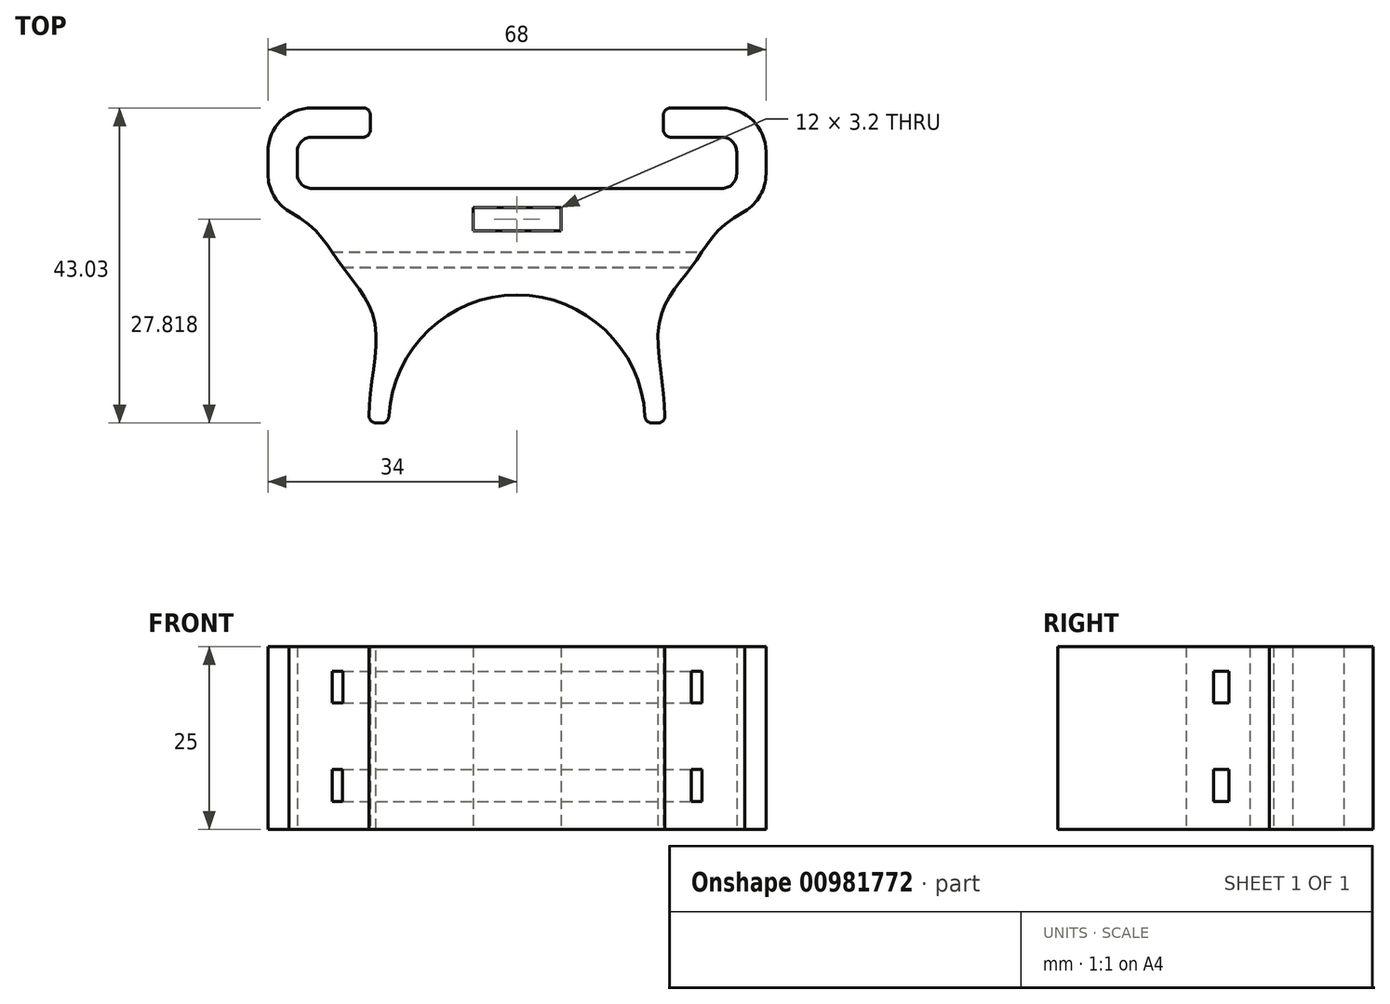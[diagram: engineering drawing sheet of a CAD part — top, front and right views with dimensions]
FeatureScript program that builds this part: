
annotation { "Feature Type Name" : "Feature", "Feature Type Description" : "" }
export const myFeature = defineFeature(function(context is Context, id is Id, definition is map)
    precondition{}
    {
        {
            var Q0;
            Q0=qCreatedBy(makeId("Top.planeOp"),FACE);
            var sketch = newSketch(context, id + "F0", { "sketchPlane" : qUnion([Q0])});
            skLineSegment(sketch, "E0", {"start": v(0, 0) * mm, "end": v(28, 0) * mm});
            skLineSegment(sketch, "E1", {"start": v(30, 2) * mm, "end": v(30, 5) * mm});
            skLineSegment(sketch, "E2", {"start": v(28, 7) * mm, "end": v(21, 7) * mm});
            skPoint(sketch, "E3.visualSharp", {"position": v(30, 7) * mm});
            skArc(sketch, "E3.filletArc", {"start": v(30, 5) * mm, "mid": v(29.41, 6.41) * mm, "end": v(28, 7) * mm});
            skPoint(sketch, "E4.visualSharp", {"position": v(30, 0) * mm});
            skArc(sketch, "E4.filletArc", {"start": v(28, 0) * mm, "mid": v(29.41, 0.59) * mm, "end": v(30, 2) * mm});
            skLineSegment(sketch, "E5.0", {"start": v(28, 11) * mm, "end": v(21, 11) * mm});
            skArc(sketch, "E5.2", {"start": v(31.12, -3.13) * mm, "mid": v(33.23, -0.94) * mm, "end": v(34, 2) * mm});
            skLineSegment(sketch, "E5.3", {"start": v(34, 2) * mm, "end": v(34, 5) * mm});
            skArc(sketch, "E5.4", {"start": v(34, 5) * mm, "mid": v(32.24, 9.24) * mm, "end": v(28, 11) * mm});
            skLineSegment(sketch, "E6", {"start": v(20, 10) * mm, "end": v(20, 8) * mm});
            skPoint(sketch, "E7.visualSharp", {"position": v(20, 11) * mm});
            skArc(sketch, "E7.filletArc", {"start": v(21, 11) * mm, "mid": v(20.3, 10.7) * mm, "end": v(20, 10) * mm});
            skPoint(sketch, "E8.visualSharp", {"position": v(20, 7) * mm});
            skArc(sketch, "E8.filletArc", {"start": v(20, 8) * mm, "mid": v(20.3, 7.3) * mm, "end": v(21, 7) * mm});
            skArc(sketch, "E9", {"start": v(17.47, -31.08) * mm, "mid": v(12.04, -19.32) * mm, "end": v(0, -14.53) * mm});
            skLineSegment(sketch, "E10", {"start": v(18.47, -32.03) * mm, "end": v(19.2, -32.03) * mm});
            skFitSpline(sketch, "E11", {"points": [v(20.16, -32.03) * mm, v(19.44, -18.28) * mm, v(24.17, -10.26) * mm, v(31.12, -3.13) * mm], "startDerivative": vector(2.72, 32.22) * mm, "endDerivative": vector(38.57, 19.7) * mm});
            skPoint(sketch, "E12.visualSharp", {"position": v(17.5, -32.03) * mm});
            skArc(sketch, "E12.filletArc", {"start": v(17.47, -31.08) * mm, "mid": v(17.79, -31.75) * mm, "end": v(18.47, -32.03) * mm});
            skArc(sketch, "E13.filletArc", {"start": v(19.2, -32.03) * mm, "mid": v(19.9, -31.74) * mm, "end": v(20.2, -31.03) * mm});
            skLineSegment(sketch, "E14.bottom", {"start": v(0, -2.61) * mm, "end": v(6, -2.61) * mm});
            skLineSegment(sketch, "E14.right", {"start": v(6, -2.61) * mm, "end": v(6, -5.81) * mm});
            skLineSegment(sketch, "E15", {"start": v(0, 0) * mm, "end": v(0, -2.61) * mm});
            skArc(sketch, "E16.MirrorCS", {"start": v(-19.2, -32.03) * mm, "mid": v(-19.9, -31.74) * mm, "end": v(-20.2, -31.03) * mm});
            skLineSegment(sketch, "E17.MirrorCS", {"start": v(-18.47, -32.03) * mm, "end": v(-19.2, -32.03) * mm});
            skArc(sketch, "E18.MirrorCS", {"start": v(-17.47, -31.08) * mm, "mid": v(-17.79, -31.75) * mm, "end": v(-18.47, -32.03) * mm});
            skArc(sketch, "E19.MirrorCS", {"start": v(-20, 8) * mm, "mid": v(-20.3, 7.3) * mm, "end": v(-21, 7) * mm});
            skLineSegment(sketch, "E20.MirrorCS", {"start": v(-20, 10) * mm, "end": v(-20, 8) * mm});
            skArc(sketch, "E21.MirrorCS", {"start": v(-21, 11) * mm, "mid": v(-20.3, 10.7) * mm, "end": v(-20, 10) * mm});
            skArc(sketch, "E22.MirrorCS", {"start": v(-30, 5) * mm, "mid": v(-29.41, 6.41) * mm, "end": v(-28, 7) * mm});
            skArc(sketch, "E23.MirrorCS", {"start": v(-28, 0) * mm, "mid": v(-29.41, 0.59) * mm, "end": v(-30, 2) * mm});
            skLineSegment(sketch, "E24.MirrorCS", {"start": v(-34, 2) * mm, "end": v(-34, 5) * mm});
            skArc(sketch, "E25.MirrorCS", {"start": v(-31.12, -3.13) * mm, "mid": v(-33.23, -0.94) * mm, "end": v(-34, 2) * mm});
            skArc(sketch, "E26.MirrorCS", {"start": v(-34, 5) * mm, "mid": v(-32.24, 9.24) * mm, "end": v(-28, 11) * mm});
            skPoint(sketch, "E27.MirrorP", {"position": v(-17.5, -32.03) * mm});
            skPoint(sketch, "E28.MirrorP", {"position": v(-30, 7) * mm});
            skLineSegment(sketch, "E29.MirrorCS", {"start": v(-6, -2.61) * mm, "end": v(-6, -5.81) * mm});
            skLineSegment(sketch, "E30.MirrorCS", {"start": v(-28, 7) * mm, "end": v(-21, 7) * mm});
            skLineSegment(sketch, "E31.MirrorCS", {"start": v(0, 0) * mm, "end": v(-28, 0) * mm});
            skPoint(sketch, "E32.MirrorP", {"position": v(-20, 7) * mm});
            skPoint(sketch, "E33.MirrorP", {"position": v(-20, 11) * mm});
            skLineSegment(sketch, "E34.MirrorCS", {"start": v(-30, 2) * mm, "end": v(-30, 5) * mm});
            skPoint(sketch, "E35.MirrorP", {"position": v(-30, 0) * mm});
            skArc(sketch, "E36.MirrorCS", {"start": v(-17.47, -31.08) * mm, "mid": v(-12.04, -19.32) * mm, "end": v(0, -14.53) * mm});
            skPoint(sketch, "E37.MirrorP", {"position": v(-20.16, -32.03) * mm});
            skLineSegment(sketch, "E38.MirrorCS", {"start": v(0, -2.61) * mm, "end": v(-6, -2.61) * mm});
            skFitSpline(sketch, "E39.MirrorCS", {"points": [v(-20.16, -32.03) * mm, v(-19.44, -18.28) * mm, v(-24.17, -10.26) * mm, v(-31.12, -3.13) * mm], "startDerivative": vector(-2.72, 32.22) * mm, "endDerivative": vector(-38.57, 19.7) * mm});
            skLineSegment(sketch, "E40.MirrorCS", {"start": v(-28, 11) * mm, "end": v(-21, 11) * mm});
            skLineSegment(sketch, "E41", {"start": v(6, -5.81) * mm, "end": v(-6, -5.81) * mm});
            skSolve(sketch);
        }
        {
            var Q0;
            Q0 = qSketchRegion(id + "F0", true);
            extrude(context, id + "F1", {"entities" : qUnion([Q0]), "depth" : 25 * mm, "offsetDistance" : 25 * mm});
        }
        {
            var Q0;
            Q0=qCreatedBy(makeId("Right.planeOp"),FACE);
            cPlane(context, id + "F2", {"entities" : qUnion([Q0]), "cplaneType" : CPlaneType.OFFSET, "offset" : 25 * mm, "width" : 150 * mm, "height" : 150 * mm});
        }
        {
            var Q0;
            Q0=qCreatedBy(id+"F2.planeOp",FACE);
            var sketch = newSketch(context, id + "F3", { "sketchPlane" : qUnion([Q0])});
            skLineSegment(sketch, "E42.bottom", {"start": v(-8.67, 3.84) * mm, "end": v(-10.76, 3.84) * mm});
            skLineSegment(sketch, "E42.top", {"start": v(-8.67, 8.2) * mm, "end": v(-10.76, 8.2) * mm});
            skLineSegment(sketch, "E42.left", {"start": v(-8.67, 3.84) * mm, "end": v(-8.67, 8.2) * mm});
            skLineSegment(sketch, "E42.right", {"start": v(-10.76, 3.84) * mm, "end": v(-10.76, 8.2) * mm});
            skLineSegment(sketch, "E43.bottom", {"start": v(-8.7, 17.28) * mm, "end": v(-10.78, 17.28) * mm});
            skLineSegment(sketch, "E43.top", {"start": v(-8.7, 21.64) * mm, "end": v(-10.78, 21.64) * mm});
            skLineSegment(sketch, "E43.left", {"start": v(-8.7, 17.28) * mm, "end": v(-8.7, 21.64) * mm});
            skLineSegment(sketch, "E43.right", {"start": v(-10.78, 17.28) * mm, "end": v(-10.78, 21.64) * mm});
            skSolve(sketch);
        }
        {
            var Q0;
            Q0=makeQuery(id+"F3.imprint","IMPRINT",FACE,{"disambiguationData":[TD([[makeQuery(id+"F3.imprint","IMPRINT",EDGE,{"derivedFrom":sQuery(id+"F3.wireOp",EDGE,"E43.bottom")}),-1.0]])]});
            var Q1;
            Q1=makeQuery(id+"F3.imprint","IMPRINT",FACE,{"disambiguationData":[TD([[makeQuery(id+"F3.imprint","IMPRINT",EDGE,{"derivedFrom":sQuery(id+"F3.wireOp",EDGE,"E42.bottom")}),-1.0]])]});
            extrude(context, id + "F4", {"entities" : qUnion([Q0, Q1]), "operationType" : NewBodyOperationType.REMOVE, "endBound" : BoundingType.THROUGH_ALL, "oppositeDirection" : true, "depth" : 65 * mm, "offsetDistance" : 25 * mm, "hasSecondDirection" : true, "secondDirectionOppositeDirection" : false, "secondDirectionDepth" : 25 * mm});
        }
    });
